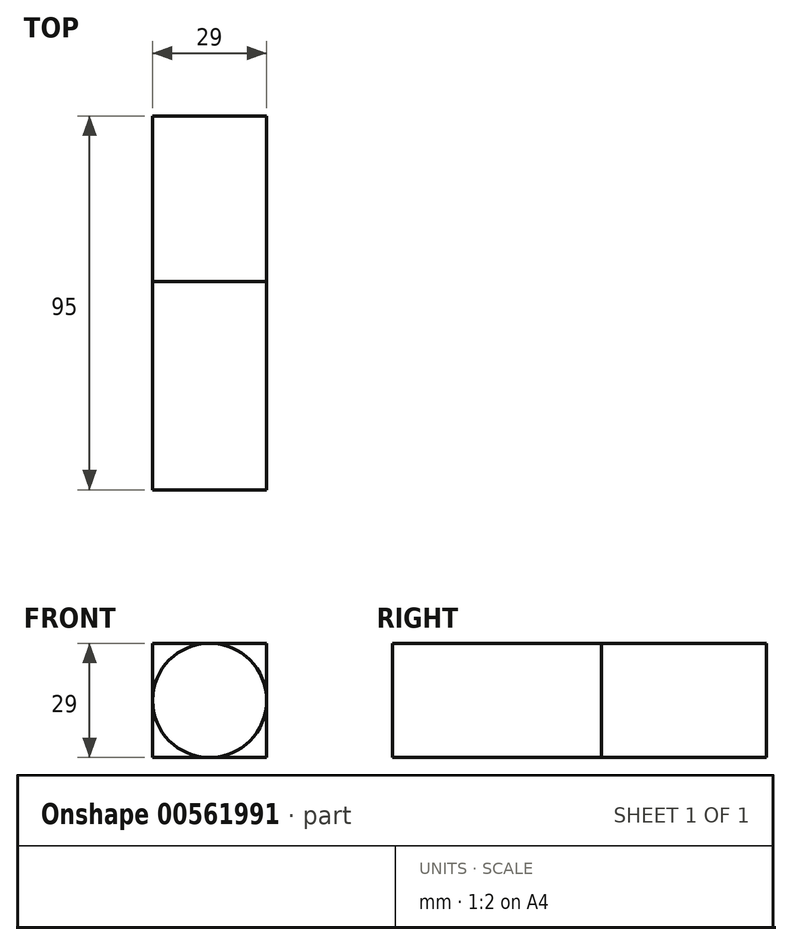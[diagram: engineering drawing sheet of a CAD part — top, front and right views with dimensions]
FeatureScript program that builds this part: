
annotation { "Feature Type Name" : "Feature", "Feature Type Description" : "" }
export const myFeature = defineFeature(function(context is Context, id is Id, definition is map)
    precondition{}
    {
        {
            var Q0;
            Q0=qCreatedBy(makeId("Top.planeOp"),FACE);
            var sketch = newSketch(context, id + "F0", { "sketchPlane" : qUnion([Q0])});
            skLineSegment(sketch, "E0.bottom", {"start": v(-14.5, 21) * mm, "end": v(14.5, 21) * mm});
            skLineSegment(sketch, "E0.top", {"start": v(-14.5, -21) * mm, "end": v(14.5, -21) * mm});
            skLineSegment(sketch, "E0.left", {"start": v(-14.5, 21) * mm, "end": v(-14.5, -21) * mm});
            skLineSegment(sketch, "E0.right", {"start": v(14.5, 21) * mm, "end": v(14.5, -21) * mm});
            skPoint(sketch, "E0.middle", {"position": v(0, 0) * mm});
            skSolve(sketch);
        }
        {
            var Q0;
            Q0=makeQuery(id+"F0.imprint","IMPRINT",FACE,{"disambiguationData":[TD([[makeQuery(id+"F0.imprint","IMPRINT",EDGE,{"derivedFrom":sQuery(id+"F0.wireOp",EDGE,"E0.bottom")}),-1.0]])]});
            extrude(context, id + "F1", {"entities" : qUnion([Q0]), "depth" : 29 * mm, "offsetDistance" : 25 * mm});
        }
        {
            var Q0;
            Q0=makeQuery(id+"F1.opExtrude","SWEPT_FACE",FACE,{"disambiguationData":[OSD([sQuery(id+"F0.wireOp",EDGE,"E0.top")])]});
            var sketch = newSketch(context, id + "F2", { "sketchPlane" : qUnion([Q0])});
            skCircle(sketch, "E1", {"center": v(0, 14.5) * mm, "radius": 14.5 * mm});
            skPoint(sketch, "E1.centerSnap0", {"position": v(-14.5, 14.5) * mm});
            skSolve(sketch);
        }
        {
            var Q0;
            {var subQ0=sQuery(id+"F2.wireOp",EDGE,"E1");var subQ1=sQuery(id+"F0.wireOp",EDGE,"E0.top");var subQ2=makeQuery(id+"F2.imprint","INTERSECT",VERTEX,{"derivedFrom":[makeQuery(id+"F1.opExtrude","CAP_EDGE",EDGE,{"disambiguationData":[OSD([subQ1])],"isStart":false}),subQ0]});Q0=makeQuery(id+"F2.imprint","IMPRINT",FACE,{"disambiguationData":[TD([[makeQuery(id+"F2.imprint","IMPRINT",EDGE,{"disambiguationData":[TD([[subQ2,1.0]])],"derivedFrom":subQ0}),1.0]])]});}
            extrude(context, id + "F3", {"entities" : qUnion([Q0]), "operationType" : NewBodyOperationType.ADD, "depth" : 12 * mm, "offsetDistance" : 25 * mm});
        }
        {
            var Q0;
            Q0=makeQuery(id+"F3.opExtrude","CAP_FACE",FACE,{"disambiguationData":[OSD([sQuery(id+"F2.wireOp",EDGE,"E1")])],"isStart":false});
            var sketch = newSketch(context, id + "F4", { "sketchPlane" : qUnion([Q0])});
            skCircle(sketch, "E2", {"center": v(0, 14.5) * mm, "radius": 15 * mm});
            skSolve(sketch);
        }
        {
            var Q0;
            Q0=makeQuery(id+"F4.imprint","IMPRINT",FACE,{"disambiguationData":[TD([[makeQuery(id+"F4.imprint","IMPRINT",EDGE,{"derivedFrom":makeQuery(id+"F3.opExtrude","CAP_EDGE",EDGE,{"disambiguationData":[OSD([sQuery(id+"F2.wireOp",EDGE,"E1")])],"isStart":false})}),1.0]])]});
            extrude(context, id + "F5", {"entities" : qUnion([Q0]), "operationType" : NewBodyOperationType.ADD, "depth" : 41 * mm, "offsetDistance" : 25 * mm});
        }
        {
            var Q0;
            Q0=makeQuery(id+"F1.opExtrude","CAP_FACE",FACE,{"disambiguationData":[OSD([sQuery(id+"F0.wireOp",EDGE,"E0.bottom"),sQuery(id+"F0.wireOp",EDGE,"E0.top"),sQuery(id+"F0.wireOp",EDGE,"E0.left"),sQuery(id+"F0.wireOp",EDGE,"E0.right")])],"isStart":true});
            var sketch = newSketch(context, id + "F6", { "sketchPlane" : qUnion([Q0])});
            skLineSegment(sketch, "E3.bottom", {"start": v(-6, 16.5) * mm, "end": v(6, 16.5) * mm});
            skLineSegment(sketch, "E3.top", {"start": v(-6, -5.5) * mm, "end": v(6, -5.5) * mm});
            skLineSegment(sketch, "E3.left", {"start": v(-6, 16.5) * mm, "end": v(-6, -5.5) * mm});
            skLineSegment(sketch, "E3.right", {"start": v(6, 16.5) * mm, "end": v(6, -5.5) * mm});
            skCircle(sketch, "E4", {"center": v(-6, 16.5) * mm, "radius": 1 * mm});
            skCircle(sketch, "E5", {"center": v(6, 16.5) * mm, "radius": 1 * mm});
            skCircle(sketch, "E6", {"center": v(-6, -5.5) * mm, "radius": 1 * mm});
            skCircle(sketch, "E7", {"center": v(6, -5.5) * mm, "radius": 1 * mm});
            skSolve(sketch);
        }
        {
            var Q0;
            Q0=sQuery(id+"F6.wireOp",EDGE,"E5");
            var Q1;
            Q1=sQuery(id+"F6.wireOp",EDGE,"E4");
            var Q2;
            Q2=sQuery(id+"F6.wireOp",EDGE,"E6");
            var Q3;
            Q3=sQuery(id+"F6.wireOp",EDGE,"E7");
            extrude(context, id + "F7", {"bodyType" : ToolBodyType.SURFACE, "operationType" : NewBodyOperationType.REMOVE, "surfaceEntities" : qUnion([Q0, Q1, Q2, Q3]), "oppositeDirection" : true, "depth" : 2 * mm, "offsetDistance" : 25 * mm});
        }
        {
            var Q0;
            Q0=makeQuery(id+"F5.opExtrude","CAP_FACE",FACE,{"disambiguationData":[OSD([sQuery(id+"F2.wireOp",EDGE,"E1")])],"isStart":false});
            cPlane(context, id + "F8", {"entities" : qUnion([Q0]), "cplaneType" : CPlaneType.OFFSET, "offset" : 3000 * mm, "width" : 150 * mm, "height" : 150 * mm});
        }
    });
